# Revit family: Genie_Site_ScissorLift_GS2632_000
name_source: partatom
category: Site
revit_build: Autodesk Revit 2017 (Build: 20160225_1515(x64)
units: mm (PartAtom-declared; Revit-internal decimal feet)

## family parameters
Always vertical = Yes
Cut with Voids When Loaded = No
OmniClass Number = 23.50.85.17.11
OmniClass Title = Electric and Battery Telescoping Platforms
Part Type = Normal
Round Connector Dimension = Use Diameter
Shared = No
Work Plane-Based = No

## types (1)
- GS-2632
    Assembly Code = E1030900
    AssetType = Fixed
    BIMObjectName = Genie_Site_ScissorLift_GS2632
    ClassificationName = Uniclass2015
    ClassificationValue = Pr_65_80_47_95
    Color = Grey & Blue
    Cost = 0 $
    Description = Ideal for maneuvering in tight spaces, the quiet, zero emission electric Genie® GS™-2632 slab scissor lift is excellent for indoor and outdoor construction, maintenance and installation applications on ﬁrm, level surfaces.
    DocumentationLiterature = https://www.genielift.com
    DocumentationTechnical = https://www.genielift.com
    DurationUnit = Years
    ExpectedLife = 0
    Features = Large platform workspace with 36-in (.9 m) roll-out platform extension. High-angle steering for excellent maneuverability. Folding rails with half-height swing gate come standard. Emergency stop at both platform and ground controls for added safety.
    Finish = Painted Steel
    IfcExportAs = IfcTransportElement
    IfcExportType = IfcTransportElementType
    Keynote = X
    Manufacturer = Genie
    ManufacturerName = Genie
    Material = Painted Steel
    Model = Genie - Scissor Lift
    ModelNumber = GS-2632
    ModelReference = Genie - Scissor Lift
    NBSDescription = Vertical lifting platforms
    NBSObjectName = Genie - Vertical lifting platforms
    NBSReference = 90-80-65/350
    NominalDepth = 810 mm
    NominalHeight = 2500 mm  [stored 8.2021 ft]
    NominalLength = 2440 mm  [stored 8.00525 ft]
    PrimaryMaterial = Steel, Paint Finish, Blue, Genie
    ProductionYear = 2018
    ReplacementCost = 0
    SecondaryMaterial = Steel, Paint Finish, Grey, Genie
    Size = 810mm x 2500mm x 2440mm
    Type Comments = GS-2632
    TypeName = Genie - Scissor Lift
    URL = http://www.genielift.co.uk
    WarrantyDurationLabor = 0
    WarrantyDurationParts = 0
    WarrantyDurationUnit = Years
    WarrantyGuarantorLabor = http://www.genielift.co.uk
    WarrantyGuarantorParts = http://www.genielift.co.uk
    _BSBibleVersion = 15
    _BimSpecGuid = 0
    _CurrentRevision = 1
    _DistributedBy = www.bimstore.co.uk

note: [stored X ft] marks values corroborated as IEEE doubles in the binary element streams (Revit-internal decimal feet)

## geometry (parser evidence)
native form markers: Sweep x15
no freeform markers — native parametric forms only
